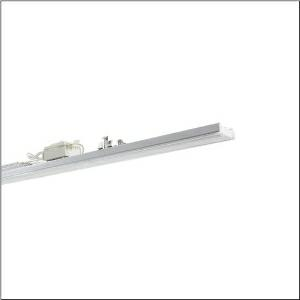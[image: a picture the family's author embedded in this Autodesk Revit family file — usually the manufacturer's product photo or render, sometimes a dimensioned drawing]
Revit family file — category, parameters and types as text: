
# Revit family: licross_r__11_recessed_extreme_mo_51te12dv4fxge_8f4a
name_source: partatom
category: Lighting Fixtures
units: mm (PartAtom-declared; Revit-internal decimal feet)

## family parameters
Cut with Voids When Loaded = No
Host = Face
Light Source = No
Part Type = Normal
Room Calculation Point = No
Round Connector Dimension = Use Diameter
Shared = No

## types (1)
- --- (1 x LED, 15360 lm, 84.1 W, 4000K)
    Apparent Load = 84 VA
    CIE Flux Codes = 67 92 99 100 100
    Color Rendering = 80
    Color Temperature = 4000K
    Default Elevation = 1800 mm
    Description = Licross® 11 Recessed extreme MO, luminaire insert, of sheet steel, galvanised, coil coated, white, length: 2.250mm, width: 66mm, height: 67mm, LED rated luminous flux: 15.360lm, light colour: 840, control gear: DALI 2, with plug, 5-pole, with phase selection, mains connection: 220..240V, AC, 50/60Hz, rated input power: 84W, halogen-free wiring, primary optical cover: cover, of PMMA, light emission: direct distribution, primary light characteristic: symmetric, protection rating (complete): IP54, insulation class (complete): insulation class I (protective earthing), certification: CE, ENEC, VDE, UKCA, protection symbol: D if used in an environment with non-conductive dust loads with corresponding accessories, impact resistance: IK06, permissible ambient temperature for indoor applications: -40..+45°C, corresponds to IFS (International Featured Standards) requirements for safety and quality in the food industry, reducing of maximum allowable ambient temperature of 5°C with ceiling mounting, LABS conformity tested according to VDMA 24364:2018-05, packaging unit: 1 piece
    Height = 58 mm
    Lamp = 1 x LED
    Lamp Light Flux = 15360 lm
    Lamp Power = 84.1 W
    Lamp count = 1
    Length = 2250 mm
    Luminous efficacy = 183 lm/W
    Manufacturer = Siteco
    ModVariant = No
    Model = 51TE12DV4FXGE
    Mounting Place = Ceiling
    Mounting Type = Pendant
    Number of Poles = 1
    OnlyDefault = Yes
    Power Factor = 1
    Product Name = Licross® 11 Recessed extreme MO
    Product group = luminaire insert
    ProductGroupID = 902
    Protection Class = Protection class I
    Protection Degree = IP 54
    RLX_Detail_Level = 1
    RLX_Emergency_Light_Flux = 0 lm
    RLX_Emergency_Type = 0
    RLX_Emergency_Type_DB = No
    RlxData = <blob elided: 29533 chars, md5=8e6bca76>
    Socket = socket
    Standby Power = 0 W
    System Light Flux = 15360 lm
    System Power = 84 W
    Type Comments = factory setting: luminous flux: 100 % | dim-lin: 254 | 378 mA
    Type Image = l_1296930.jpg
    URL = http://relux.com
    VarID = @adj_082446
    Voltage = 0 V
    Weight = 0.00 kg
    Width = 66 mm

## geometry (parser evidence)
native form markers: Blend x4, Sweep x10
no freeform markers — native parametric forms only
